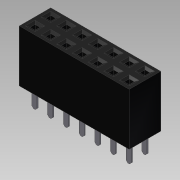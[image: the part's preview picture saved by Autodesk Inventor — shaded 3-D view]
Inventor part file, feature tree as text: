
AUTODESK INVENTOR PART (.ipt)
format: ipt  version: 2011 (Build 150239000, 239)  size: 261,120 bytes
history: native  units: mm
features: sketch x6, extrude x4, other x2, pattern_linear x2, loft x1, projected_geometry x1
ambient origin geometry x8: Origin, YZ Plane, XZ Plane, XY Plane, X Axis, Y Axis, Z Axis, Center Point
feature tree (16):
  other  "Твердое тело1"
  extrude  "Выдавливание1"  Depth=17.78mm
  extrude  "Выдавливание2"  Depth=5.08mm
  extrude  "Выдавливание3"  Depth=8.89mm
  pattern_linear  "Прямоуг.массив1"  Spacing1=2.54mm  [1 undecoded]
  sketch  "Эскиз4"
  other  "РабПлоскость1"
  loft  "По сечениям1"
  extrude  "Выдавливание4"  Depth=0.2mm
  pattern_linear  "Прямоуг.массив2"  Spacing1=0.8mm  [1 undecoded]
  sketch  "Эскиз1"
  sketch  "Эскиз2"
  sketch  "Эскиз3"
  projected_geometry  "Спроецированная петля1"
  sketch  "Эскиз5"
  sketch  "Эскиз6"
note: 2 required parameter values undecoded (feature->parameter linkage not recoverable at this tier; creation-order binding heuristic only, values carry confidence <= 0.55)
